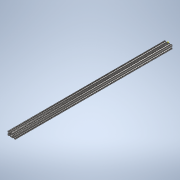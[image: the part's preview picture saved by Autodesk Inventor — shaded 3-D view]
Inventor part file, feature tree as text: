
AUTODESK INVENTOR PART (.ipt)
format: ipt  version: 2020 (Build 240168000, 168)  size: 350,720 bytes
history: native  units: in
note: dims shown in document units (in); Inventor stores cm internally (conversion verified against a paired STEP export)
features: sketch x2, extrude x1
ambient origin geometry x8: Origin, YZ Plane, XZ Plane, XY Plane, X Axis, Y Axis, Z Axis, Center Point
bodies: Solid1 (feature_tree)
feature tree (3):
  extrude  "Extrusion1"  [1 undecoded]
  sketch  "Sketch2"
  sketch  "Sketch1"  dims[d0=40.0in d1=0.0in]
note: 1 required parameter value undecoded (feature->parameter linkage not recoverable at this tier; creation-order binding heuristic only, values carry confidence <= 0.55)
